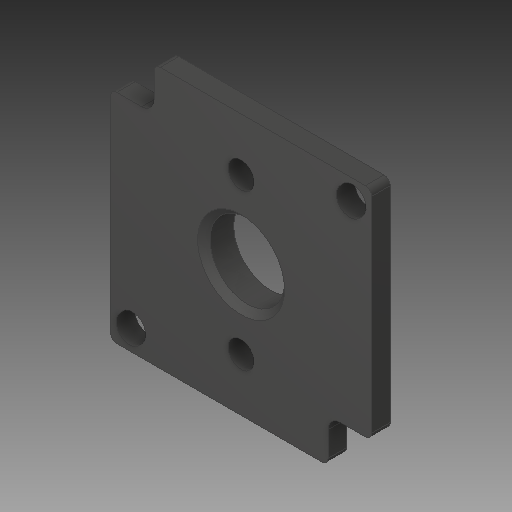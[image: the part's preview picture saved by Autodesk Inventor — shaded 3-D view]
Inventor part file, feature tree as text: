
AUTODESK INVENTOR PART (.ipt)
format: ipt  version: 2017 (Build 210142000, 142)  size: 219,136 bytes
history: native  units: in
note: dims shown in document units (in); Inventor stores cm internally (conversion verified against a paired STEP export)
features: fillet x1
ambient origin geometry x8: Origin, YZ Plane, XZ Plane, XY Plane, X Axis, Y Axis, Z Axis, Center Point
bodies: Solid1 (feature_tree)
feature tree (1):
  fillet  "Fillet4"  [1 undecoded]
note: 1 required parameter value undecoded (feature->parameter linkage not recoverable at this tier; creation-order binding heuristic only, values carry confidence <= 0.55)
